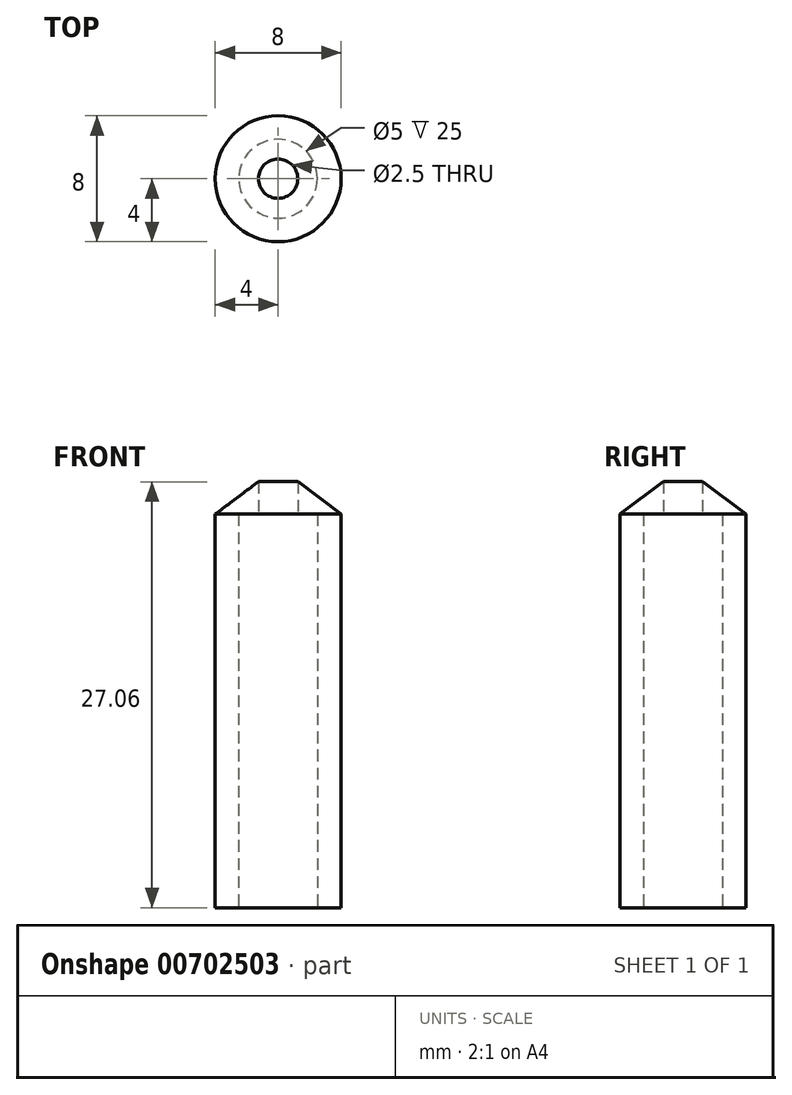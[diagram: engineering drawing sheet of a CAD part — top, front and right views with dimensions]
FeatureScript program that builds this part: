
annotation { "Feature Type Name" : "Feature", "Feature Type Description" : "" }
export const myFeature = defineFeature(function(context is Context, id is Id, definition is map)
    precondition{}
    {
        {
            var Q0;
            Q0=qCreatedBy(makeId("Front.planeOp"),FACE);
            var sketch = newSketch(context, id + "F0", { "sketchPlane" : qUnion([Q0])});
            skLineSegment(sketch, "E0", {"start": v(0, 0) * mm, "end": v(4, 0) * mm});
            skLineSegment(sketch, "E1", {"start": v(4, 0) * mm, "end": v(4, 25) * mm});
            skLineSegment(sketch, "E2", {"start": v(4, 25) * mm, "end": v(0, 25) * mm});
            skLineSegment(sketch, "E3", {"start": v(0, 0) * mm, "end": v(0, 25) * mm});
            skLineSegment(sketch, "E4", {"start": v(0, 25) * mm, "end": v(0, 28) * mm});
            skLineSegment(sketch, "E5", {"start": v(0, 28) * mm, "end": v(4, 25) * mm});
            skSolve(sketch);
        }
        {
            var Q0;
            Q0=makeQuery(id+"F0.imprint","IMPRINT",FACE,{"disambiguationData":[TD([[makeQuery(id+"F0.imprint","IMPRINT",EDGE,{"derivedFrom":sQuery(id+"F0.wireOp",EDGE,"E0")}),1.0]])]});
            var Q1;
            Q1=makeQuery(id+"F0.imprint","IMPRINT",FACE,{"disambiguationData":[TD([[makeQuery(id+"F0.imprint","IMPRINT",EDGE,{"derivedFrom":sQuery(id+"F0.wireOp",EDGE,"E2")}),-1.0]])]});
            var Q2;
            Q2=sQuery(id+"F0.wireOp",EDGE,"E3");
            revolve(context, id + "F1", {"entities" : qUnion([Q0, Q1]), "axis" : qUnion([Q2]), "revolveType" : RevolveType.FULL});
        }
        {
            var Q0;
            Q0=makeQuery(id+"F1.opRevolve","SWEPT_FACE",FACE,{"disambiguationData":[OSD([sQuery(id+"F0.wireOp",EDGE,"E0")])]});
            var sketch = newSketch(context, id + "F2", { "sketchPlane" : qUnion([Q0])});
            skCircle(sketch, "E6", {"center": v(0, 0) * mm, "radius": 2.5 * mm});
            skSolve(sketch);
        }
        {
            var Q0;
            Q0=makeQuery(id+"F2.imprint","IMPRINT",FACE,{"disambiguationData":[TD([[makeQuery(id+"F2.imprint","IMPRINT",EDGE,{"derivedFrom":sQuery(id+"F2.wireOp",EDGE,"E6")}),1.0]])]});
            extrude(context, id + "F3", {"entities" : qUnion([Q0]), "operationType" : NewBodyOperationType.REMOVE, "oppositeDirection" : true, "depth" : 25 * mm, "offsetDistance" : 25 * mm});
        }
        {
            var Q0;
            Q0=makeQuery(id+"F3.boolean.opBoolean","COPY",FACE,{"derivedFrom":makeQuery(id+"F3.opExtrude","CAP_FACE",FACE,{"disambiguationData":[OSD([sQuery(id+"F2.wireOp",EDGE,"E6")])],"isStart":false})});
            var sketch = newSketch(context, id + "F4", { "sketchPlane" : qUnion([Q0])});
            skCircle(sketch, "E7", {"center": v(0, 0) * mm, "radius": 1.25 * mm});
            skSolve(sketch);
        }
        {
            var Q0;
            Q0=makeQuery(id+"F4.imprint","IMPRINT",FACE,{"disambiguationData":[TD([[makeQuery(id+"F4.imprint","IMPRINT",EDGE,{"derivedFrom":sQuery(id+"F4.wireOp",EDGE,"E7")}),1.0]])]});
            extrude(context, id + "F5", {"entities" : qUnion([Q0]), "operationType" : NewBodyOperationType.REMOVE, "oppositeDirection" : true, "depth" : 25 * mm, "offsetDistance" : 25 * mm});
        }
    });
